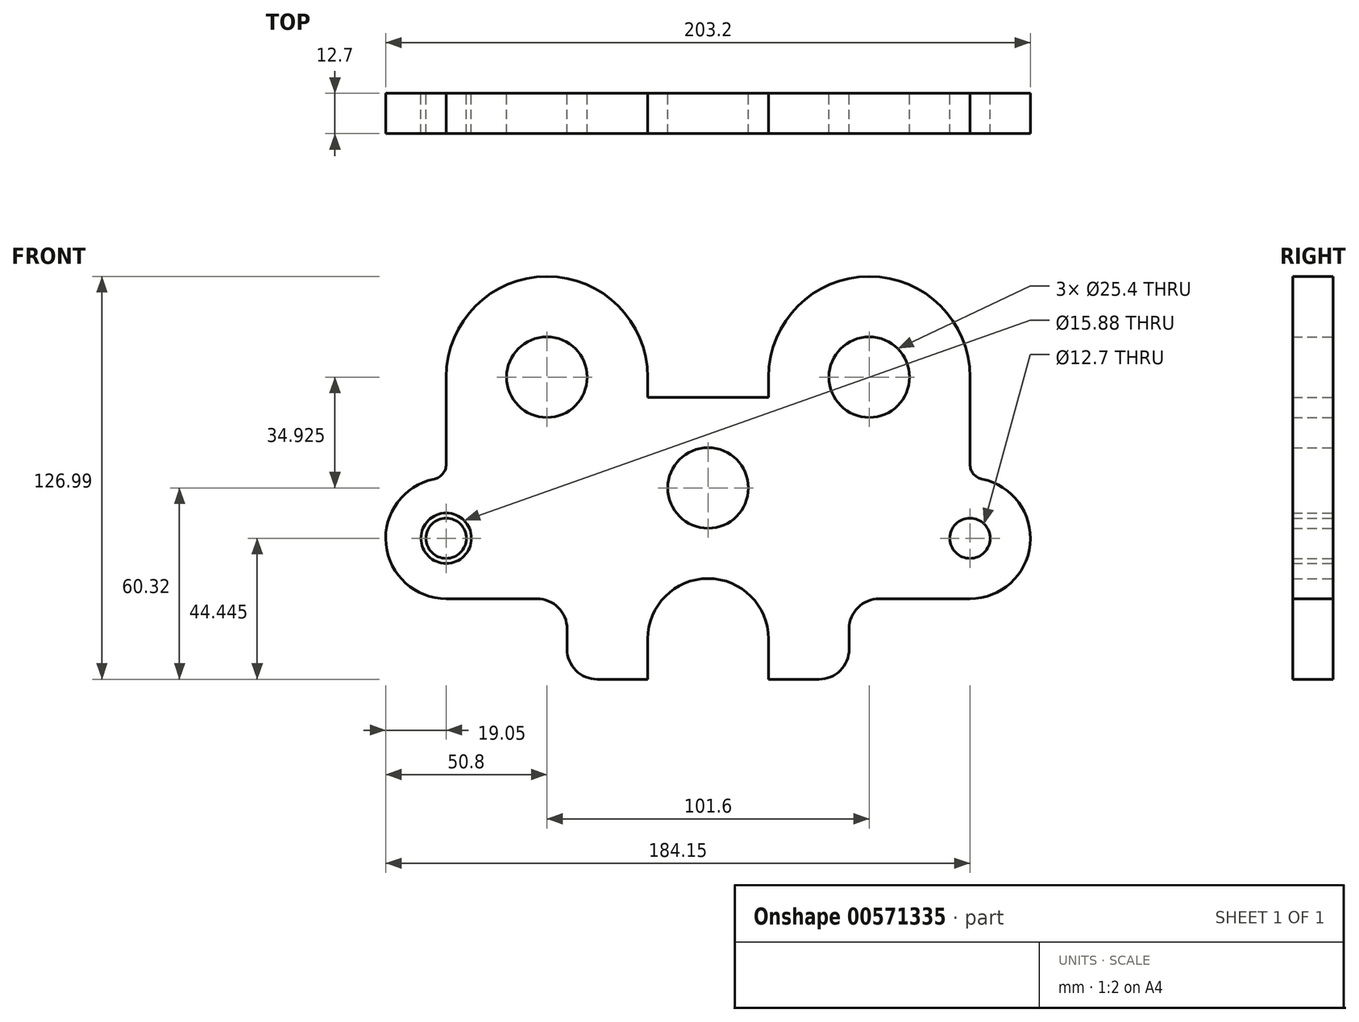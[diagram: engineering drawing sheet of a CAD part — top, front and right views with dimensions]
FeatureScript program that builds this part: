
annotation { "Feature Type Name" : "Feature", "Feature Type Description" : "" }
export const myFeature = defineFeature(function(context is Context, id is Id, definition is map)
    precondition{}
    {
        {
            var Q0;
            Q0=qCreatedBy(makeId("Front.planeOp"),FACE);
            var sketch = newSketch(context, id + "F0", { "sketchPlane" : qUnion([Q0])});
            skLineSegment(sketch, "E0", {"start": v(50.8, 46.36) * mm, "end": v(50.8, 0) * mm, "construction": true});
            skLineSegment(sketch, "E1", {"start": v(0, 34.93) * mm, "end": v(62.77, 34.93) * mm, "construction": true});
            skLineSegment(sketch, "E2", {"start": v(0, 47.1) * mm, "end": v(0, -90.6) * mm, "construction": true});
            skLineSegment(sketch, "E3", {"start": v(0, 0) * mm, "end": v(100.31, 0) * mm, "construction": true});
            skLineSegment(sketch, "E4.MirrorCS", {"start": v(0, 34.93) * mm, "end": v(-62.77, 34.93) * mm, "construction": true});
            skLineSegment(sketch, "E5.MirrorCS", {"start": v(0, 0) * mm, "end": v(-100.31, 0) * mm, "construction": true});
            skCircle(sketch, "E6", {"center": v(50.8, 34.93) * mm, "radius": 12.7 * mm});
            skCircle(sketch, "E7", {"center": v(0, 0) * mm, "radius": 12.7 * mm});
            skPoint(sketch, "E8.startSnap0", {"position": v(31.38, 34.93) * mm});
            skLineSegment(sketch, "E9", {"start": v(19.05, 28.57) * mm, "end": v(19.05, 34.93) * mm});
            skArc(sketch, "E10", {"start": v(82.55, 34.93) * mm, "mid": v(50.8, 66.68) * mm, "end": v(19.05, 34.93) * mm});
            skLineSegment(sketch, "E11", {"start": v(82.55, 34.93) * mm, "end": v(82.55, 7.46) * mm});
            skLineSegment(sketch, "E12", {"start": v(70.06, -15.88) * mm, "end": v(102.63, -15.88) * mm, "construction": true});
            skLineSegment(sketch, "E13", {"start": v(82.55, -9.84) * mm, "end": v(82.55, -41.13) * mm, "construction": true});
            skPoint(sketch, "E14", {"position": v(82.55, -15.87) * mm});
            skCircle(sketch, "E15", {"center": v(82.55, -15.87) * mm, "radius": 6.35 * mm});
            skLineSegment(sketch, "E16", {"start": v(19.05, 28.57) * mm, "end": v(-23.18, 28.57) * mm});
            skArc(sketch, "E17", {"start": v(82.55, -34.92) * mm, "mid": v(101.5, -17.79) * mm, "end": v(86.36, 2.8) * mm});
            skLineSegment(sketch, "E18", {"start": v(82.55, -34.92) * mm, "end": v(53.98, -34.92) * mm});
            skLineSegment(sketch, "E19", {"start": v(44.45, -44.45) * mm, "end": v(44.45, -50.8) * mm});
            skLineSegment(sketch, "E20", {"start": v(34.93, -60.32) * mm, "end": v(19.05, -60.32) * mm});
            skLineSegment(sketch, "E21", {"start": v(19.05, -60.32) * mm, "end": v(19.05, -47.62) * mm});
            skLineSegment(sketch, "E22", {"start": v(-32.06, -47.62) * mm, "end": v(27.67, -47.62) * mm, "construction": true});
            skArc(sketch, "E23", {"start": v(19.05, -47.62) * mm, "mid": v(0, -28.57) * mm, "end": v(-19.05, -47.63) * mm});
            skLineSegment(sketch, "E24.MirrorCS", {"start": v(-19.05, 28.57) * mm, "end": v(-19.05, 34.92) * mm});
            skArc(sketch, "E25.MirrorCS", {"start": v(-82.55, 34.92) * mm, "mid": v(-50.8, 66.68) * mm, "end": v(-19.05, 34.92) * mm});
            skLineSegment(sketch, "E26.MirrorCS", {"start": v(-82.55, 34.92) * mm, "end": v(-82.55, 7.46) * mm});
            skArc(sketch, "E27.MirrorCS", {"start": v(-82.55, -34.92) * mm, "mid": v(-101.5, -17.79) * mm, "end": v(-86.36, 2.8) * mm});
            skCircle(sketch, "E28.MirrorC", {"center": v(-82.55, -15.87) * mm, "radius": 6.35 * mm});
            skCircle(sketch, "E29.MirrorC", {"center": v(-50.8, 34.93) * mm, "radius": 12.7 * mm});
            skLineSegment(sketch, "E30.MirrorCS", {"start": v(-82.55, -34.93) * mm, "end": v(-53.97, -34.92) * mm});
            skLineSegment(sketch, "E31.MirrorCS", {"start": v(-44.45, -44.45) * mm, "end": v(-44.45, -50.8) * mm});
            skLineSegment(sketch, "E32.MirrorCS", {"start": v(-34.93, -60.32) * mm, "end": v(-19.05, -60.32) * mm});
            skLineSegment(sketch, "E33.MirrorCS", {"start": v(-19.05, -60.33) * mm, "end": v(-19.05, -47.63) * mm});
            skLineSegment(sketch, "E34.MirrorCS", {"start": v(-82.55, -9.84) * mm, "end": v(-82.55, -41.13) * mm, "construction": true});
            skLineSegment(sketch, "E35.MirrorCS", {"start": v(-50.8, 46.36) * mm, "end": v(-50.8, 0) * mm, "construction": true});
            skLineSegment(sketch, "E36.MirrorCS", {"start": v(-70.06, -15.88) * mm, "end": v(-102.63, -15.88) * mm, "construction": true});
            skPoint(sketch, "E37.visualSharp", {"position": v(-82.55, 3.17) * mm});
            skArc(sketch, "E37.filletArc", {"start": v(-86.36, 2.8) * mm, "mid": v(-83.62, 4.44) * mm, "end": v(-82.55, 7.46) * mm});
            skPoint(sketch, "E38.visualSharp", {"position": v(82.55, 3.17) * mm});
            skArc(sketch, "E38.filletArc", {"start": v(82.55, 7.46) * mm, "mid": v(83.62, 4.44) * mm, "end": v(86.36, 2.8) * mm});
            skPoint(sketch, "E39.visualSharp", {"position": v(-44.45, -34.92) * mm});
            skArc(sketch, "E39.filletArc", {"start": v(-44.45, -44.45) * mm, "mid": v(-47.24, -37.71) * mm, "end": v(-53.97, -34.92) * mm});
            skPoint(sketch, "E40.visualSharp", {"position": v(44.45, -34.92) * mm});
            skArc(sketch, "E40.filletArc", {"start": v(53.98, -34.92) * mm, "mid": v(47.24, -37.71) * mm, "end": v(44.45, -44.45) * mm});
            skPoint(sketch, "E41.visualSharp", {"position": v(-44.45, -60.32) * mm});
            skArc(sketch, "E41.filletArc", {"start": v(-44.45, -50.8) * mm, "mid": v(-41.66, -57.54) * mm, "end": v(-34.93, -60.32) * mm});
            skPoint(sketch, "E42.visualSharp", {"position": v(44.45, -60.32) * mm});
            skArc(sketch, "E42.filletArc", {"start": v(34.93, -60.32) * mm, "mid": v(41.66, -57.54) * mm, "end": v(44.45, -50.8) * mm});
            skCircle(sketch, "E43", {"center": v(82.55, -15.87) * mm, "radius": 7.94 * mm});
            skCircle(sketch, "E44.MirrorC", {"center": v(-82.55, -15.87) * mm, "radius": 7.94 * mm});
            skSolve(sketch);
        }
        {
            var Q0;
            Q0=qSketchRegion(id+"F0",true);
            var Q1;
            Q1=makeQuery(id+"F0.imprint","IMPRINT",FACE,{"disambiguationData":[TD([[makeQuery(id+"F0.imprint","IMPRINT",EDGE,{"derivedFrom":sQuery(id+"F0.wireOp",EDGE,"E15")}),-1.0]])]});
            var Q2;
            Q2=makeQuery(id+"F0.imprint","IMPRINT",FACE,{"disambiguationData":[TD([[makeQuery(id+"F0.imprint","IMPRINT",EDGE,{"derivedFrom":sQuery(id+"F0.wireOp",EDGE,"E28.MirrorC")}),1.0]])]});
            extrude(context, id + "F1", {"entities" : qUnion([Q0, Q1, Q2]), "endBound" : BoundingType.SYMMETRIC, "depth" : 12.7 * mm, "offsetDistance" : 25.4 * mm});
        }
    });
